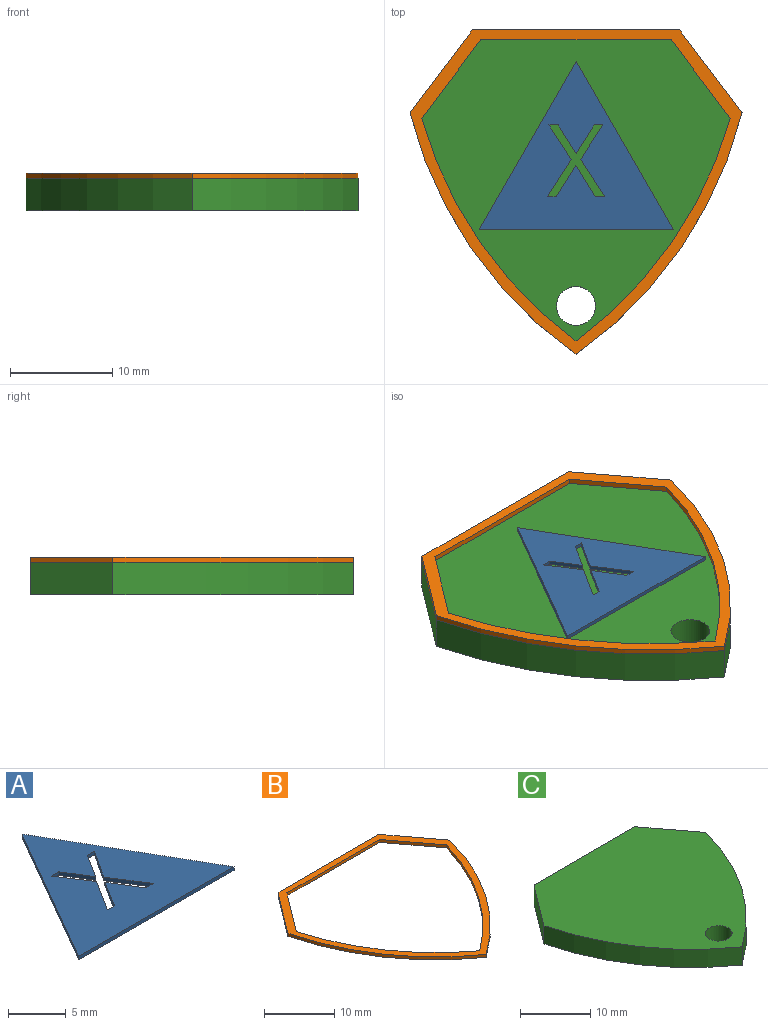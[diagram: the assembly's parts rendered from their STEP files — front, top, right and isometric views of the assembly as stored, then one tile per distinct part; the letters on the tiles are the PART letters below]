
ASSEMBLY  parts=3 mates=2
PART A: 17 faces, bbox 19.1x16.5x0.4 mm
  f0: plane 19.05x0.38mm, normal (0,-1,0), area 7.3mm2, adj f1,f14,f15,f16
  f1: plane 16.5x9.53mm, normal (0.87,0.5,0), area 7.3mm2, adj f0,f14,f15,f16
  f2: plane 3.71x2.35mm, normal (-0.84,-0.54,0), area 1.7mm2, adj f3,f13,f15,f16
  f3: plane 0.93x0.38mm, normal (0,1,0), area 0.4mm2, adj f2,f4,f15,f16
  f4: plane 3.1x1.89mm, normal (0.85,0.52,0), area 1.4mm2, adj f3,f5,f15,f16
  f5: plane 3.1x1.93mm, normal (-0.85,0.53,0), area 1.4mm2, adj f4,f6,f15,f16
  f6: plane 0.87x0.38mm, normal (0,1,0), area 0.3mm2, adj f5,f7,f15,f16
  f7: plane 3.68x2.34mm, normal (0.84,-0.54,0), area 1.7mm2, adj f6,f8,f15,f16
  f8: plane 3.36x2.18mm, normal (0.84,0.54,0), area 1.5mm2, adj f7,f9,f15,f16
  f9: plane 0.91x0.38mm, normal (0,-1,0), area 0.3mm2, adj f8,f10,f15,f16
  f10: plane 2.79x1.75mm, normal (-0.85,-0.53,0), area 1.3mm2, adj f9,f11,f15,f16
  f11: plane 2.79x1.76mm, normal (0.85,-0.53,0), area 1.3mm2, adj f10,f12,f15,f16
  f12: plane 0.87x0.38mm, normal (0,-1,0), area 0.3mm2, adj f11,f13,f15,f16
  f13: plane 3.34x2.18mm, normal (-0.84,0.55,0), area 1.5mm2, adj f2,f12,f15,f16
  f14: plane 16.5x9.53mm, normal (-0.87,0.5,0), area 7.3mm2, adj f0,f1,f15,f16
  f15: plane 19.05x16.5mm, normal (0,0,1), area 145.5mm2, adj f0,f1,f2,f3,f4,f5,f6,f7
  f16: plane 19.05x16.5mm, normal (0,0,-1), area 145.5mm2, adj f0,f1,f2,f3,f4,f5,f6,f7
PART B: 12 faces, bbox 32.5x31.8x0.5 mm
  f0: plane 20.32x0.51mm, normal (0,1,0), area 10.3mm2, adj f1,f9,f10,f11
  f1: plane 8.12x6.11mm, normal (-0.8,0.6,0), area 5.2mm2, adj f0,f2,f10,f11
  f2: cylinder r=40.99mm len=23.63mm, axis (0,0,-1), area 14.9mm2, adj f1,f3,f10,f11
  f3: cylinder r=40.99mm len=23.63mm, axis (0,0,-1), area 14.9mm2, adj f2,f9,f10,f11
  f4: plane 18.66x0.51mm, normal (0,-1,0), area 9.5mm2, adj f5,f8,f10,f11
  f5: plane 7.7x5.79mm, normal (-0.8,-0.6,0), area 4.9mm2, adj f4,f6,f10,f11
  f6: cylinder r=40.9mm len=21.82mm, axis (0,0,-1), area 13.7mm2, adj f5,f7,f10,f11
  f7: cylinder r=40.9mm len=21.82mm, axis (0,0,-1), area 13.7mm2, adj f6,f8,f10,f11
  f8: plane 7.7x5.79mm, normal (0.8,-0.6,0), area 4.9mm2, adj f4,f7,f10,f11
  f9: plane 8.12x6.11mm, normal (0.8,0.6,0), area 5.2mm2, adj f0,f3,f10,f11
  f10: plane 32.54x31.75mm, normal (0,0,1), area 101.8mm2, adj f0,f1,f2,f3,f4,f5,f6,f7
  f11: plane 32.54x31.75mm, normal (0,0,-1), area 101.8mm2, adj f0,f1,f2,f3,f4,f5,f6,f7
PART C: 8 faces, bbox 32.5x31.8x3.2 mm
  f0: plane 20.32x3.18mm, normal (0,1,0), area 64.5mm2, adj f1,f5,f6,f7
  f1: plane 8.12x6.11mm, normal (-0.8,0.6,0), area 32.3mm2, adj f0,f2,f6,f7
  f2: cylinder r=40.99mm len=23.63mm, axis (0,0,-1), area 93.1mm2, adj f1,f3,f6,f7
  f3: cylinder r=40.99mm len=23.63mm, axis (0,0,-1), area 93.1mm2, adj f2,f5,f6,f7
  f4: cylinder r=1.91mm len=3.81mm, axis (0,0,-1), area 38mm2, adj f6,f7
  f5: plane 8.12x6.11mm, normal (0.8,0.6,0), area 32.3mm2, adj f0,f3,f6,f7
  f6: plane 32.54x31.75mm, normal (0,0,1), area 687.4mm2, adj f0,f1,f2,f3,f4,f5
  f7: plane 32.54x31.75mm, normal (0,0,-1), area 687.4mm2, adj f0,f1,f2,f3,f4,f5
PLACE A t=(6.29,20.81,-2.71)mm
PLACE B t=(15.79,8.6,-2.71)mm
PLACE C t=(15.79,40.35,-5.88)mm
MATE fastened A.f16 <-> C.f6  axis (0,0,-1) through (15.79,27.51,-2.71)mm
MATE fastened B.f11 <-> C.f6  axis (0,0,-1) through (15.79,40.35,-2.71)mm
